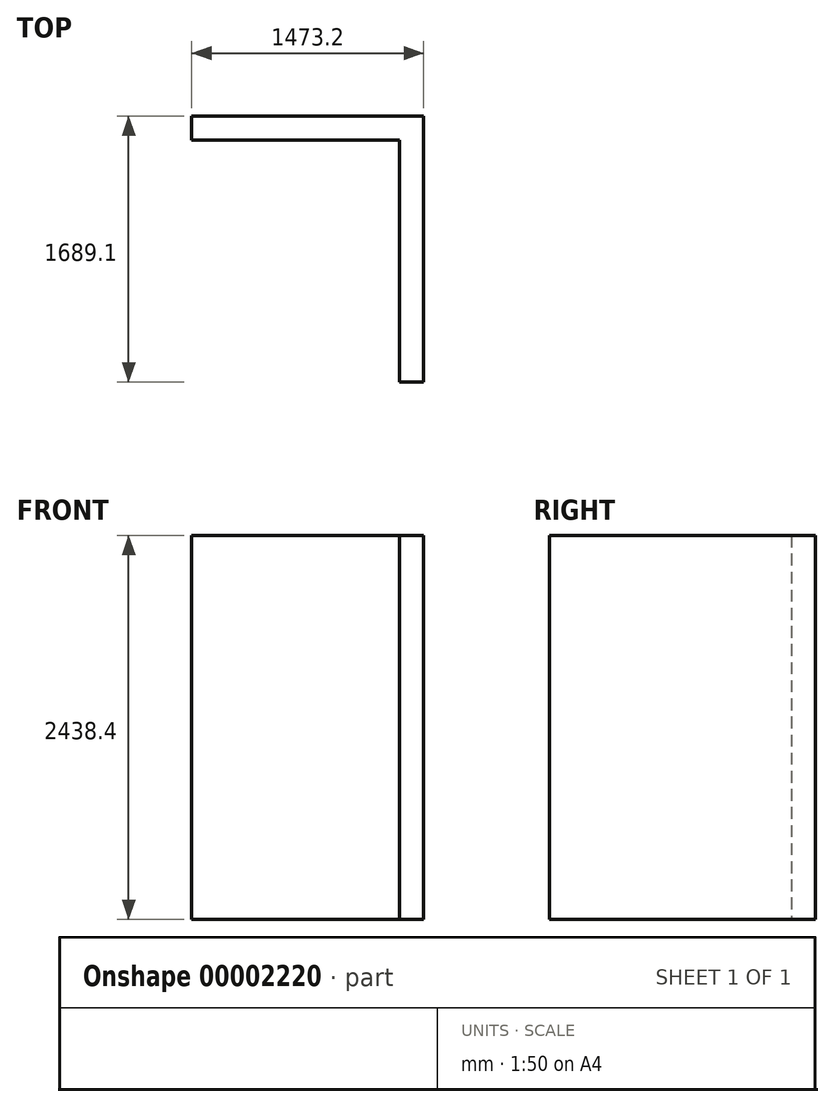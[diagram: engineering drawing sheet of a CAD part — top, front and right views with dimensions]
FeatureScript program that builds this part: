
annotation { "Feature Type Name" : "Feature", "Feature Type Description" : "" }
export const myFeature = defineFeature(function(context is Context, id is Id, definition is map)
    precondition{}
    {
        {
            var Q0;
            Q0=qCreatedBy(makeId("Top.planeOp"),FACE);
            var sketch = newSketch(context, id + "F0", { "sketchPlane" : qUnion([Q0])});
            skLineSegment(sketch, "E0", {"start": v(0, 0) * mm, "end": v(-1320.8, 0) * mm});
            skLineSegment(sketch, "E1", {"start": v(0, 0) * mm, "end": v(0, -1536.7) * mm});
            skLineSegment(sketch, "E2", {"start": v(-1320.8, 0) * mm, "end": v(-1320.8, 152.4) * mm});
            skLineSegment(sketch, "E3", {"start": v(-1320.8, 152.4) * mm, "end": v(152.4, 152.4) * mm});
            skLineSegment(sketch, "E4", {"start": v(0, -1536.7) * mm, "end": v(152.4, -1536.7) * mm});
            skLineSegment(sketch, "E5", {"start": v(152.4, -1536.7) * mm, "end": v(152.4, 152.4) * mm});
            skSolve(sketch);
        }
        {
            var Q0;
            Q0=makeQuery(id+"F0.imprint","IMPRINT",FACE,{"disambiguationData":[TD([[makeQuery(id+"F0.imprint","IMPRINT",EDGE,{"derivedFrom":sQuery(id+"F0.wireOp",EDGE,"E0")}),-1.0]])]});
            var Q1;
            Q1=sQuery(id+"F0.wireOp",EDGE,"E0");
            var Q2;
            Q2=sQuery(id+"F0.wireOp",EDGE,"E1");
            extrude(context, id + "F1", {"entities" : qUnion([Q0]), "surfaceEntities" : qUnion([Q1, Q2]), "depth" : 2438.4 * mm});
        }
        {
            var Q0;
            Q0=makeQuery(id+"F1.opExtrude","SWEPT_FACE",FACE,{"disambiguationData":[OSD([sQuery(id+"F0.wireOp",EDGE,"E0")])]});
            var sketch = newSketch(context, id + "F2", { "sketchPlane" : qUnion([Q0])});
            skLineSegment(sketch, "E6", {"start": v(-1016, 762) * mm, "end": v(-101.6, 762) * mm});
            skSolve(sketch);
        }
        {
            var Q0;
            Q0=makeQuery(id+"F1.opExtrude","SWEPT_FACE",FACE,{"disambiguationData":[OSD([sQuery(id+"F0.wireOp",EDGE,"E1")])]});
            var sketch = newSketch(context, id + "F3", { "sketchPlane" : qUnion([Q0])});
            skLineSegment(sketch, "E7", {"start": v(101.6, 762) * mm, "end": v(1016, 762) * mm});
            skSolve(sketch);
        }
    });
